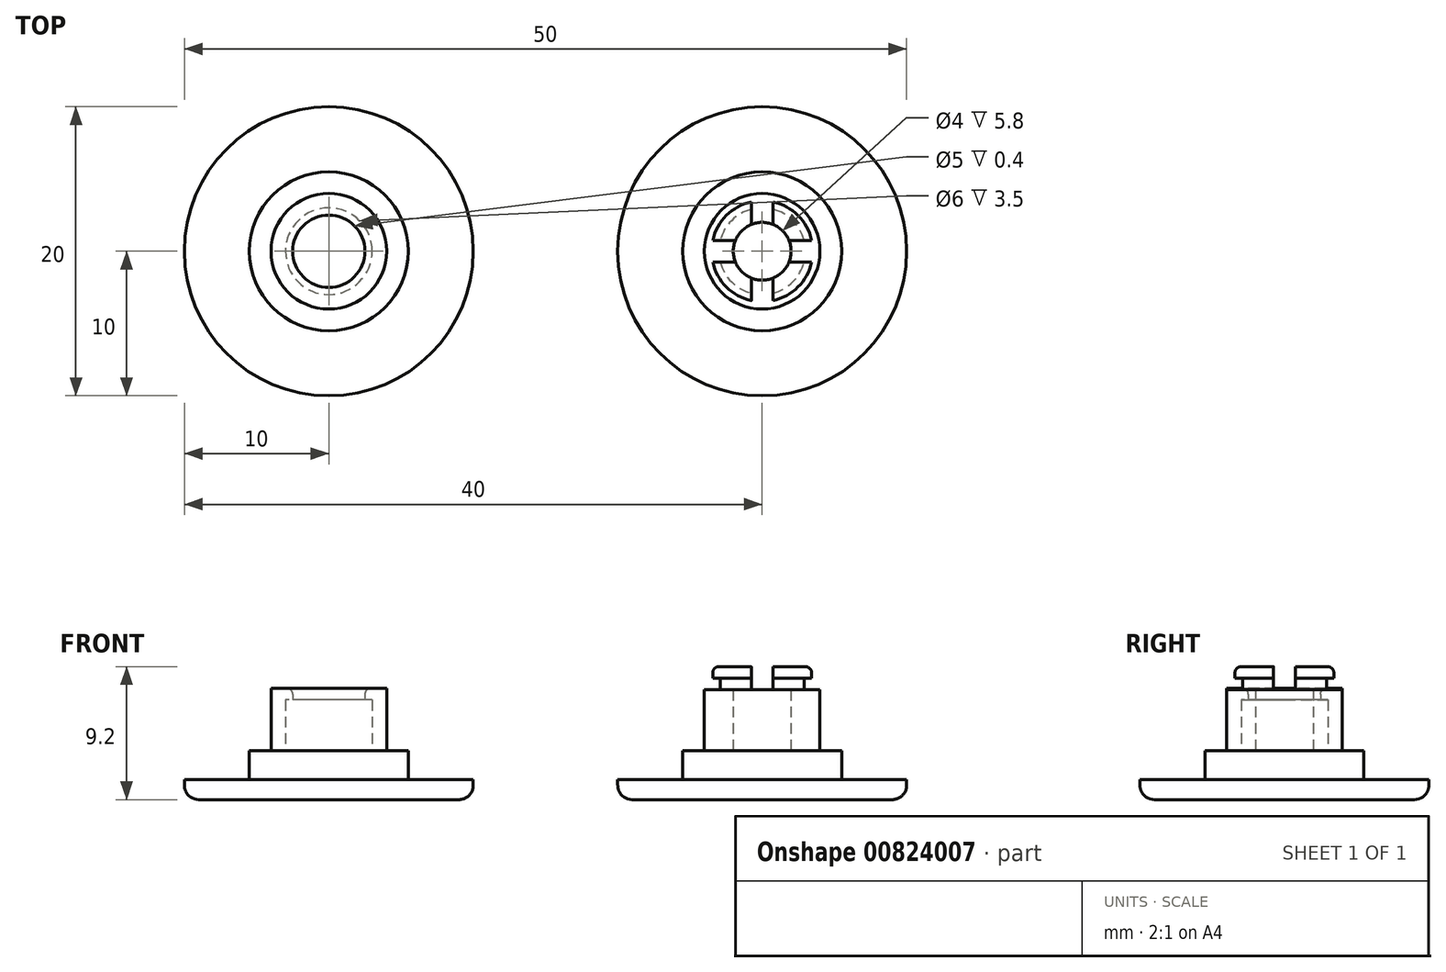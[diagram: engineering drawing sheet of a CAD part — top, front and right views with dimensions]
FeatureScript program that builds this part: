
annotation { "Feature Type Name" : "Feature", "Feature Type Description" : "" }
export const myFeature = defineFeature(function(context is Context, id is Id, definition is map)
    precondition{}
    {
        {
            var Q0;
            Q0=qCreatedBy(makeId("Top.planeOp"),FACE);
            var sketch = newSketch(context, id + "F0", { "sketchPlane" : qUnion([Q0])});
            skCircle(sketch, "E0", {"center": v(0, 0) * mm, "radius": 10 * mm});
            skSolve(sketch);
        }
        {
            var Q0;
            Q0=makeQuery(id+"F0.imprint","IMPRINT",FACE,{"disambiguationData":[TD([[makeQuery(id+"F0.imprint","IMPRINT",EDGE,{"derivedFrom":sQuery(id+"F0.wireOp",EDGE,"E0")}),1.0]])]});
            extrude(context, id + "F1", {"entities" : qUnion([Q0]), "depth" : 1.4 * mm, "offsetDistance" : 25 * mm});
        }
        {
            var Q0;
            Q0=makeQuery(id+"F1.opExtrude","CAP_FACE",FACE,{"disambiguationData":[OSD([sQuery(id+"F0.wireOp",EDGE,"E0")])],"isStart":false});
            var sketch = newSketch(context, id + "F2", { "sketchPlane" : qUnion([Q0])});
            skCircle(sketch, "E1", {"center": v(0, 0) * mm, "radius": 5.5 * mm});
            skSolve(sketch);
        }
        {
            var Q0;
            Q0=makeQuery(id+"F2.imprint","IMPRINT",FACE,{"disambiguationData":[TD([[makeQuery(id+"F2.imprint","IMPRINT",EDGE,{"derivedFrom":sQuery(id+"F2.wireOp",EDGE,"E1")}),1.0]])]});
            extrude(context, id + "F3", {"entities" : qUnion([Q0]), "operationType" : NewBodyOperationType.ADD, "depth" : 2 * mm, "offsetDistance" : 25 * mm});
        }
        {
            var Q0;
            Q0=makeQuery(id+"F1.opExtrude","SWEPT_BODY",BODY,{"disambiguationData":[OSD([sQuery(id+"F0.wireOp",EDGE,"E0")])]});
            transform(context, id + "F4", {"entities" : qUnion([Q0]), "transformType" : TransformType.TRANSLATION_3D, "dx" : 30 * mm, "dy" : 0 * mm, "dz" : 0 * mm, "makeCopy" : true});
        }
        {
            var Q0;
            Q0=makeQuery(id+"F3.opExtrude","CAP_FACE",FACE,{"disambiguationData":[OSD([sQuery(id+"F2.wireOp",EDGE,"E1")])],"isStart":false});
            var sketch = newSketch(context, id + "F5", { "sketchPlane" : qUnion([Q0])});
            skCircle(sketch, "E2", {"center": v(0, 0) * mm, "radius": 4 * mm});
            skCircle(sketch, "E3", {"center": v(0, 0) * mm, "radius": 3 * mm});
            skSolve(sketch);
        }
        {
            var Q0;
            Q0=makeQuery(id+"F5.imprint","IMPRINT",FACE,{"disambiguationData":[TD([[makeQuery(id+"F5.imprint","IMPRINT",EDGE,{"derivedFrom":sQuery(id+"F5.wireOp",EDGE,"E2")}),1.0]])]});
            extrude(context, id + "F6", {"entities" : qUnion([Q0]), "operationType" : NewBodyOperationType.ADD, "depth" : 3.5 * mm, "offsetDistance" : 25 * mm});
        }
        {
            var Q0;
            Q0=makeQuery(id+"F6.opExtrude","CAP_FACE",FACE,{"disambiguationData":[OSD([sQuery(id+"F5.wireOp",EDGE,"E2"),sQuery(id+"F5.wireOp",EDGE,"E3")])],"isStart":false});
            var sketch = newSketch(context, id + "F7", { "sketchPlane" : qUnion([Q0])});
            skCircle(sketch, "E4", {"center": v(0, 0) * mm, "radius": 4 * mm});
            skCircle(sketch, "E5", {"center": v(0, 0) * mm, "radius": 2.5 * mm});
            skSolve(sketch);
        }
        {
            var Q0;
            Q0=makeQuery(id+"F7.imprint","IMPRINT",FACE,{"disambiguationData":[TD([[makeQuery(id+"F7.imprint","IMPRINT",EDGE,{"derivedFrom":sQuery(id+"F7.wireOp",EDGE,"E4")}),1.0]])]});
            var Q1;
            Q1=makeQuery(id+"F7.imprint","IMPRINT",FACE,{"disambiguationData":[TD([[makeQuery(id+"F7.imprint","IMPRINT",EDGE,{"derivedFrom":sQuery(id+"F7.wireOp",EDGE,"E5")}),-1.0]])]});
            extrude(context, id + "F8", {"entities" : qUnion([Q0, Q1]), "operationType" : NewBodyOperationType.ADD, "depth" : 0.8 * mm, "offsetDistance" : 25 * mm});
        }
        {
            var Q0;
            Q0=makeQuery(id+"F4.opPattern","COPY",FACE,{"derivedFrom":makeQuery(id+"F3.opExtrude","CAP_FACE",FACE,{"disambiguationData":[OSD([sQuery(id+"F2.wireOp",EDGE,"E1")])],"isStart":false}),"instanceName":"1"});
            var sketch = newSketch(context, id + "F9", { "sketchPlane" : qUnion([Q0])});
            skCircle(sketch, "E6.0", {"center": v(30, 0) * mm, "radius": 4 * mm});
            skCircle(sketch, "E7", {"center": v(30, 0) * mm, "radius": 2 * mm});
            skSolve(sketch);
        }
        {
            var Q0;
            Q0=makeQuery(id+"F9.imprint","IMPRINT",FACE,{"disambiguationData":[TD([[makeQuery(id+"F9.imprint","IMPRINT",EDGE,{"derivedFrom":sQuery(id+"F9.wireOp",EDGE,"E6.0")}),1.0]])]});
            extrude(context, id + "F10", {"entities" : qUnion([Q0]), "operationType" : NewBodyOperationType.ADD, "depth" : 4.2 * mm, "offsetDistance" : 25 * mm});
        }
        {
            var Q0;
            Q0=makeQuery(id+"F10.opExtrude","CAP_FACE",FACE,{"disambiguationData":[OSD([sQuery(id+"F9.wireOp",EDGE,"E6.0"),sQuery(id+"F9.wireOp",EDGE,"E7")])],"isStart":false});
            var sketch = newSketch(context, id + "F11", { "sketchPlane" : qUnion([Q0])});
            skCircle(sketch, "E8", {"center": v(30, 0) * mm, "radius": 2 * mm});
            skCircle(sketch, "E9", {"center": v(30, 0) * mm, "radius": 3 * mm});
            skSolve(sketch);
        }
        {
            var Q0;
            Q0=makeQuery(id+"F11.imprint","IMPRINT",FACE,{"disambiguationData":[TD([[makeQuery(id+"F11.imprint","IMPRINT",EDGE,{"derivedFrom":sQuery(id+"F11.wireOp",EDGE,"E8")}),-1.0]])]});
            var Q1;
            Q1=makeQuery(id+"F11.imprint","IMPRINT",FACE,{"disambiguationData":[TD([[makeQuery(id+"F11.imprint","IMPRINT",EDGE,{"derivedFrom":sQuery(id+"F11.wireOp",EDGE,"E9")}),1.0]])]});
            extrude(context, id + "F12", {"entities" : qUnion([Q0, Q1]), "operationType" : NewBodyOperationType.ADD, "depth" : 0.8 * mm, "offsetDistance" : 25 * mm});
        }
        {
            var Q0;
            Q0=makeQuery(id+"F12.opExtrude","CAP_FACE",FACE,{"disambiguationData":[OSD([sQuery(id+"F11.wireOp",EDGE,"E8"),sQuery(id+"F11.wireOp",EDGE,"E9")])],"isStart":false});
            var sketch = newSketch(context, id + "F13", { "sketchPlane" : qUnion([Q0])});
            skCircle(sketch, "E10", {"center": v(30, 0) * mm, "radius": 3 * mm});
            skCircle(sketch, "E11", {"center": v(30, 0) * mm, "radius": 3.5 * mm});
            skSolve(sketch);
        }
        {
            var Q0;
            Q0=makeQuery(id+"F13.imprint","IMPRINT",FACE,{"disambiguationData":[TD([[makeQuery(id+"F13.imprint","IMPRINT",EDGE,{"derivedFrom":sQuery(id+"F13.wireOp",EDGE,"E10")}),-1.0]])]});
            var Q1;
            Q1=makeQuery(id+"F13.imprint","IMPRINT",FACE,{"disambiguationData":[TD([[makeQuery(id+"F13.imprint","IMPRINT",EDGE,{"derivedFrom":sQuery(id+"F13.wireOp",EDGE,"E10")}),1.0]])]});
            extrude(context, id + "F14", {"entities" : qUnion([Q0, Q1]), "operationType" : NewBodyOperationType.ADD, "depth" : 0.8 * mm, "offsetDistance" : 25 * mm});
        }
        {
            var Q0;
            Q0=makeQuery(id+"F1.opExtrude","CAP_EDGE",EDGE,{"disambiguationData":[OSD([sQuery(id+"F0.wireOp",EDGE,"E0")])],"isStart":true});
            var Q1;
            Q1=makeQuery(id+"F4.opPattern","COPY",EDGE,{"derivedFrom":makeQuery(id+"F1.opExtrude","CAP_EDGE",EDGE,{"disambiguationData":[OSD([sQuery(id+"F0.wireOp",EDGE,"E0")])],"isStart":true}),"instanceName":"1"});
            fillet(context, id + "F15", {"entities" : qUnion([Q0, Q1]), "radius" : 1 * mm, "tangentPropagation" : true, "allowEdgeOverflow" : false});
        }
        {
            var Q0;
            Q0=makeQuery(id+"F14.opExtrude","CAP_EDGE",EDGE,{"disambiguationData":[OSD([sQuery(id+"F13.wireOp",EDGE,"E11")])],"isStart":false});
            var Q1;
            Q1=makeQuery(id+"F12.opExtrude","CAP_EDGE",EDGE,{"disambiguationData":[OSD([sQuery(id+"F11.wireOp",EDGE,"E9")])],"isStart":false});
            var Q2;
            Q2=makeQuery(id+"F8.opExtrude","CAP_EDGE",EDGE,{"disambiguationData":[OSD([sQuery(id+"F7.wireOp",EDGE,"E5")])],"isStart":false});
            var Q3;
            Q3=makeQuery(id+"F6.opExtrude","CAP_EDGE",EDGE,{"disambiguationData":[OSD([sQuery(id+"F5.wireOp",EDGE,"E3")])],"isStart":false});
            var Q4;
            Q4=makeQuery(id+"F12.opExtrude","CAP_EDGE",EDGE,{"disambiguationData":[OSD([sQuery(id+"F11.wireOp",EDGE,"E9")])],"isStart":true});
            fillet(context, id + "F16", {"entities" : qUnion([Q0, Q1, Q2, Q3, Q4]), "radius" : 0.4 * mm, "tangentPropagation" : true, "allowEdgeOverflow" : false});
        }
        {
            var Q0;
            Q0=makeQuery(id+"F14.opExtrude","CAP_FACE",FACE,{"disambiguationData":[OSD([sQuery(id+"F11.wireOp",EDGE,"E8"),sQuery(id+"F13.wireOp",EDGE,"E11")])],"isStart":false});
            var sketch = newSketch(context, id + "F17", { "sketchPlane" : qUnion([Q0])});
            skLineSegment(sketch, "E12.bottom", {"start": v(30.75, 7.57) * mm, "end": v(29.25, 7.57) * mm});
            skLineSegment(sketch, "E12.top", {"start": v(30.75, -7.57) * mm, "end": v(29.25, -7.57) * mm});
            skPoint(sketch, "E12.middle", {"position": v(30, 0) * mm});
            skLineSegment(sketch, "E13.left", {"start": v(36.6, -0.75) * mm, "end": v(36.6, 0.75) * mm});
            skLineSegment(sketch, "E13.right", {"start": v(23.4, -0.75) * mm, "end": v(23.4, 0.75) * mm});
            skPoint(sketch, "E14", {"position": v(29.25, 0.75) * mm});
            skPoint(sketch, "E15", {"position": v(30.75, 0.75) * mm});
            skPoint(sketch, "E16", {"position": v(30.75, -0.75) * mm});
            skPoint(sketch, "E17", {"position": v(29.25, -0.75) * mm});
            skLineSegment(sketch, "E18", {"start": v(29.25, 7.57) * mm, "end": v(29.25, 0.75) * mm});
            skLineSegment(sketch, "E19", {"start": v(29.25, 0.75) * mm, "end": v(23.4, 0.75) * mm});
            skLineSegment(sketch, "E20", {"start": v(23.4, -0.75) * mm, "end": v(29.25, -0.75) * mm});
            skLineSegment(sketch, "E21", {"start": v(29.25, -0.75) * mm, "end": v(29.25, -7.57) * mm});
            skLineSegment(sketch, "E22", {"start": v(30.75, -7.57) * mm, "end": v(30.75, -0.75) * mm});
            skLineSegment(sketch, "E23", {"start": v(30.75, -0.75) * mm, "end": v(36.6, -0.75) * mm});
            skLineSegment(sketch, "E24", {"start": v(36.6, 0.75) * mm, "end": v(30.75, 0.75) * mm});
            skLineSegment(sketch, "E25", {"start": v(30.75, 7.57) * mm, "end": v(30.75, 0.75) * mm});
            skSolve(sketch);
        }
        {
            var Q0;
            {var subQ0=sQuery(id+"F17.wireOp",EDGE,"E18");var subQ2=sQuery(id+"F11.wireOp",EDGE,"E8");var subQ5=makeQuery(id+"F14.opExtrude","CAP_EDGE",EDGE,{"disambiguationData":[OSD([subQ2])],"isStart":false});var subQ6=makeQuery(id+"F17.imprint","INTERSECT",VERTEX,{"derivedFrom":[subQ5,subQ0]});Q0=makeQuery(id+"F17.imprint","IMPRINT",FACE,{"disambiguationData":[TD([[makeQuery(id+"F17.imprint","IMPRINT",EDGE,{"disambiguationData":[TD([[subQ6,1.0]])],"derivedFrom":subQ5}),-1.0]])]});}
            var Q1;
            {var subQ5=sQuery(id+"F17.wireOp",EDGE,"E19");var subQ9=sQuery(id+"F17.wireOp",EDGE,"E18");var subQ10=makeQuery(id+"F17.imprint","INTERSECT",VERTEX,{"derivedFrom":[subQ9,subQ5]});Q1=makeQuery(id+"F17.imprint","IMPRINT",FACE,{"disambiguationData":[TD([[makeQuery(id+"F17.imprint","IMPRINT",EDGE,{"disambiguationData":[TD([[subQ10,1.0]])],"derivedFrom":subQ9}),1.0]])]});}
            var Q2;
            {var subQ0=sQuery(id+"F17.wireOp",EDGE,"E23");var subQ2=sQuery(id+"F11.wireOp",EDGE,"E8");var subQ5=makeQuery(id+"F14.opExtrude","CAP_EDGE",EDGE,{"disambiguationData":[OSD([subQ2])],"isStart":false});var subQ6=makeQuery(id+"F17.imprint","INTERSECT",VERTEX,{"derivedFrom":[subQ5,subQ0]});Q2=makeQuery(id+"F17.imprint","IMPRINT",FACE,{"disambiguationData":[TD([[makeQuery(id+"F17.imprint","IMPRINT",EDGE,{"disambiguationData":[TD([[subQ6,-1.0]])],"derivedFrom":subQ5}),-1.0]])]});}
            var Q3;
            {var subQ0=sQuery(id+"F17.wireOp",EDGE,"E21");var subQ2=sQuery(id+"F11.wireOp",EDGE,"E8");var subQ5=makeQuery(id+"F14.opExtrude","CAP_EDGE",EDGE,{"disambiguationData":[OSD([subQ2])],"isStart":false});var subQ6=makeQuery(id+"F17.imprint","INTERSECT",VERTEX,{"derivedFrom":[subQ5,subQ0]});Q3=makeQuery(id+"F17.imprint","IMPRINT",FACE,{"disambiguationData":[TD([[makeQuery(id+"F17.imprint","IMPRINT",EDGE,{"disambiguationData":[TD([[subQ6,-1.0]])],"derivedFrom":subQ5}),-1.0]])]});}
            var Q4;
            {var subQ0=sQuery(id+"F17.wireOp",EDGE,"E19");var subQ2=sQuery(id+"F11.wireOp",EDGE,"E8");var subQ5=makeQuery(id+"F14.opExtrude","CAP_EDGE",EDGE,{"disambiguationData":[OSD([subQ2])],"isStart":false});var subQ6=makeQuery(id+"F17.imprint","INTERSECT",VERTEX,{"derivedFrom":[subQ5,subQ0]});Q4=makeQuery(id+"F17.imprint","IMPRINT",FACE,{"disambiguationData":[TD([[makeQuery(id+"F17.imprint","IMPRINT",EDGE,{"disambiguationData":[TD([[subQ6,-1.0]])],"derivedFrom":subQ5}),-1.0]])]});}
            var Q5;
            {var subQ0=sQuery(id+"F17.wireOp",EDGE,"E13.left");Q5=makeQuery(id+"F17.imprint","IMPRINT",FACE,{"disambiguationData":[TD([[makeQuery(id+"F17.imprint","IMPRINT",EDGE,{"derivedFrom":subQ0}),1.0]])]});}
            var Q6;
            {var subQ0=sQuery(id+"F17.wireOp",EDGE,"E12.top");Q6=makeQuery(id+"F17.imprint","IMPRINT",FACE,{"disambiguationData":[TD([[makeQuery(id+"F17.imprint","IMPRINT",EDGE,{"derivedFrom":subQ0}),-1.0]])]});}
            var Q7;
            {var subQ0=sQuery(id+"F17.wireOp",EDGE,"E13.right");Q7=makeQuery(id+"F17.imprint","IMPRINT",FACE,{"disambiguationData":[TD([[makeQuery(id+"F17.imprint","IMPRINT",EDGE,{"derivedFrom":subQ0}),-1.0]])]});}
            var Q8;
            {var subQ0=sQuery(id+"F17.wireOp",EDGE,"E12.bottom");Q8=makeQuery(id+"F17.imprint","IMPRINT",FACE,{"disambiguationData":[TD([[makeQuery(id+"F17.imprint","IMPRINT",EDGE,{"derivedFrom":subQ0}),1.0]])]});}
            var Q9;
            Q9=makeQuery(id+"F10.opExtrude","CAP_FACE",FACE,{"disambiguationData":[OSD([sQuery(id+"F9.wireOp",EDGE,"E6.0"),sQuery(id+"F9.wireOp",EDGE,"E7")])],"isStart":false});
            extrude(context, id + "F18", {"entities" : qUnion([Q0, Q1, Q2, Q3, Q4, Q5, Q6, Q7, Q8]), "operationType" : NewBodyOperationType.REMOVE, "endBound" : BoundingType.UP_TO_SURFACE, "oppositeDirection" : true, "depth" : 25 * mm, "endBoundEntityFace" : qUnion([Q9]), "offsetDistance" : 25 * mm});
        }
    });
